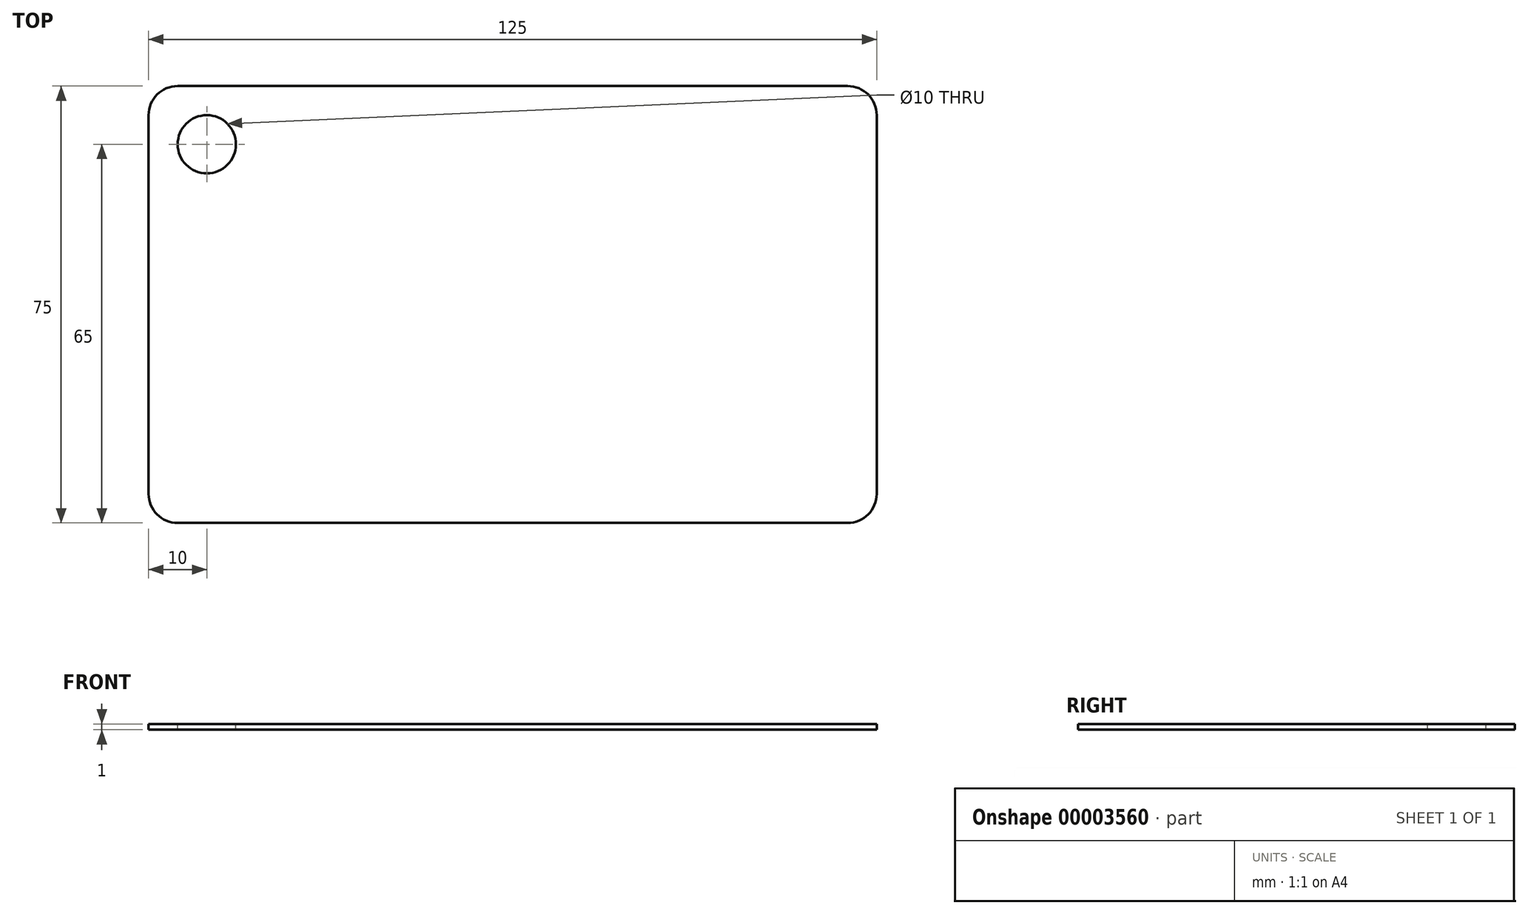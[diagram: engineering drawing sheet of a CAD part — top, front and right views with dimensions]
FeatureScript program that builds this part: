
annotation { "Feature Type Name" : "Feature", "Feature Type Description" : "" }
export const myFeature = defineFeature(function(context is Context, id is Id, definition is map)
    precondition{}
    {
        {
            var Q0;
            Q0=qCreatedBy(makeId("Top.planeOp"),FACE);
            var sketch = newSketch(context, id + "F0", { "sketchPlane" : qUnion([Q0])});
            skLineSegment(sketch, "E0", {"start": v(-62.5, 37.5) * mm, "end": v(62.5, 37.5) * mm});
            skLineSegment(sketch, "E1", {"start": v(62.5, 37.5) * mm, "end": v(62.5, -37.5) * mm});
            skLineSegment(sketch, "E2", {"start": v(62.5, -37.5) * mm, "end": v(-62.5, -37.5) * mm});
            skLineSegment(sketch, "E3", {"start": v(-62.5, -37.5) * mm, "end": v(-62.5, 37.5) * mm});
            skSolve(sketch);
        }
        {
            var Q0;
            Q0 = qSketchRegion(id + "F0", true);
            extrude(context, id + "F1", {"entities" : qUnion([Q0]), "depth" : 1 * mm});
        }
        {
            var Q0;
            Q0=makeQuery(id+"F1.opExtrude","SWEPT_EDGE",EDGE,{"disambiguationData":[OSD([sQuery(id+"F0.wireOp",EDGE,"E1"),sQuery(id+"F0.wireOp",EDGE,"E2")])]});
            var Q1;
            Q1=makeQuery(id+"F1.opExtrude","SWEPT_EDGE",EDGE,{"disambiguationData":[OSD([sQuery(id+"F0.wireOp",EDGE,"E2"),sQuery(id+"F0.wireOp",EDGE,"E3")])]});
            var Q2;
            Q2=makeQuery(id+"F1.opExtrude","SWEPT_EDGE",EDGE,{"disambiguationData":[OSD([sQuery(id+"F0.wireOp",EDGE,"E0"),sQuery(id+"F0.wireOp",EDGE,"E3")])]});
            var Q3;
            Q3=makeQuery(id+"F1.opExtrude","SWEPT_EDGE",EDGE,{"disambiguationData":[OSD([sQuery(id+"F0.wireOp",EDGE,"E0"),sQuery(id+"F0.wireOp",EDGE,"E1")])]});
            fillet(context, id + "F2", {"entities" : qUnion([Q0, Q1, Q2, Q3]), "radius" : 5 * mm, "tangentPropagation" : true, "allowEdgeOverflow" : false});
        }
        {
            var Q0;
            Q0=makeQuery(id+"F1.opExtrude","CAP_FACE",FACE,{"disambiguationData":[OSD([sQuery(id+"F0.wireOp",EDGE,"E0"),sQuery(id+"F0.wireOp",EDGE,"E1"),sQuery(id+"F0.wireOp",EDGE,"E2"),sQuery(id+"F0.wireOp",EDGE,"E3")])],"isStart":false});
            var sketch = newSketch(context, id + "F3", { "sketchPlane" : qUnion([Q0])});
            skCircle(sketch, "E4", {"center": v(-52.5, 27.5) * mm, "radius": 5 * mm});
            skSolve(sketch);
        }
        {
            var Q0;
            Q0 = qSketchRegion(id + "F3", true);
            extrude(context, id + "F4", {"entities" : qUnion([Q0]), "operationType" : NewBodyOperationType.REMOVE, "oppositeDirection" : true, "depth" : 25.4 * mm});
        }
    });
